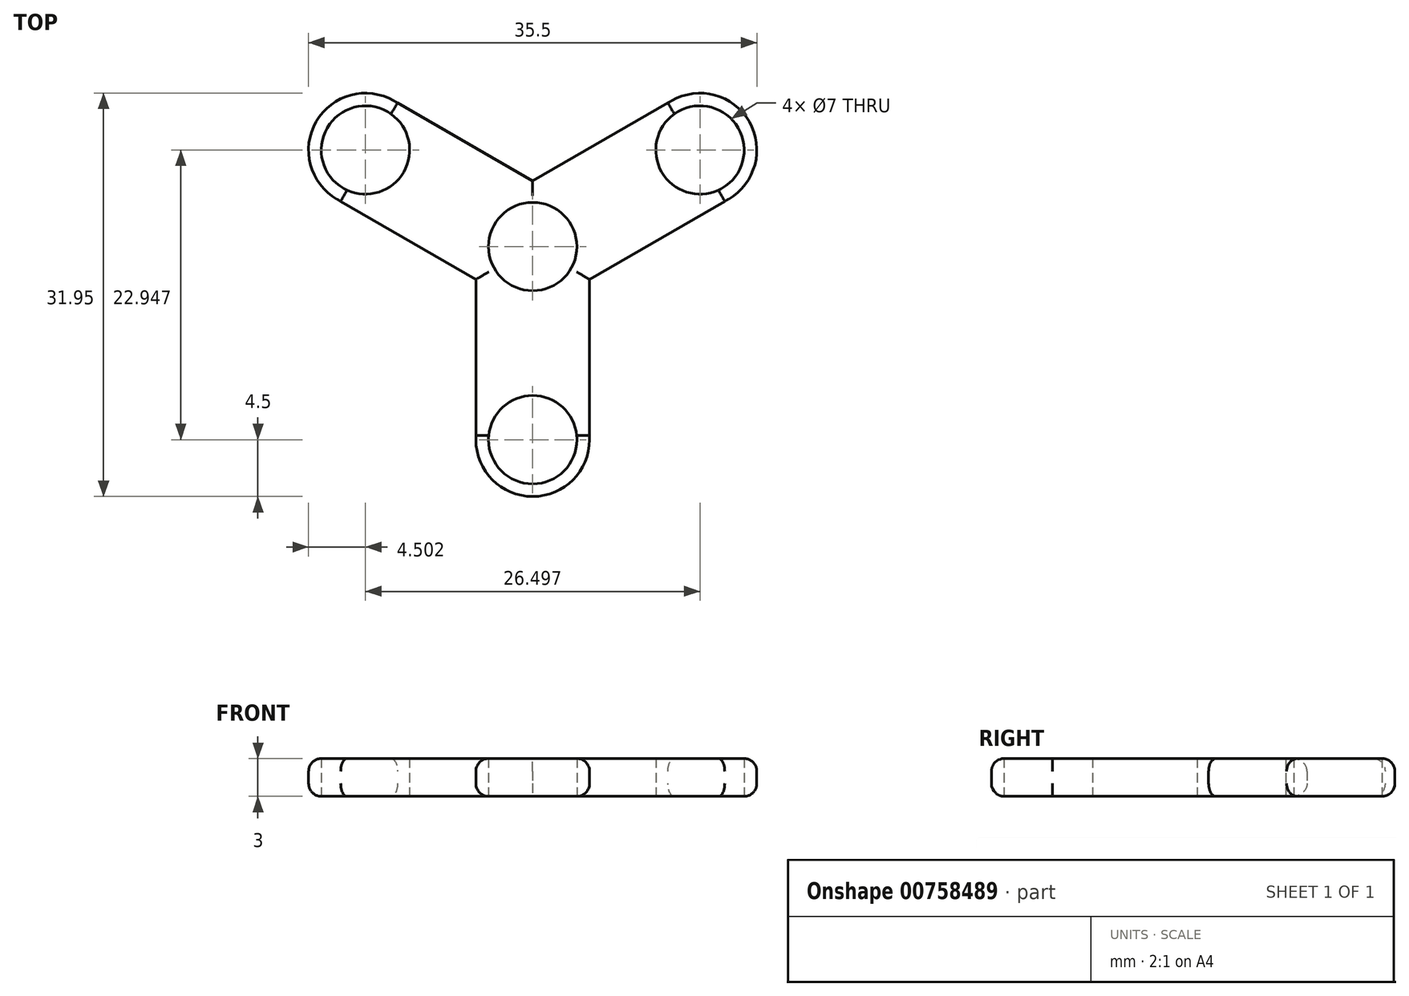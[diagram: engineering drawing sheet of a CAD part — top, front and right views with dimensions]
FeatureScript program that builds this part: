
annotation { "Feature Type Name" : "Feature", "Feature Type Description" : "" }
export const myFeature = defineFeature(function(context is Context, id is Id, definition is map)
    precondition{}
    {
        {
            var Q0;
            Q0=qCreatedBy(makeId("Top.planeOp"),FACE);
            var sketch = newSketch(context, id + "F0", { "sketchPlane" : qUnion([Q0])});
            skPoint(sketch, "E0.0.midPoint", {"position": v(6.35, -3.67) * mm});
            skLineSegment(sketch, "E1", {"start": v(-58.3, 0) * mm, "end": v(49.78, 0) * mm, "construction": true});
            skCircle(sketch, "E2", {"center": v(-13.25, 10.25) * mm, "radius": 4.5 * mm});
            skCircle(sketch, "E3", {"center": v(13.25, 10.25) * mm, "radius": 4.5 * mm});
            skCircle(sketch, "E4", {"center": v(0, -12.7) * mm, "radius": 4.5 * mm});
            skLineSegment(sketch, "E5", {"start": v(-4.5, -12.7) * mm, "end": v(-4.5, 0) * mm});
            skPoint(sketch, "E5.endSnap0", {"position": v(-4.26, 0) * mm});
            skLineSegment(sketch, "E6", {"start": v(4.5, -12.7) * mm, "end": v(4.5, 0) * mm});
            skLineSegment(sketch, "E7", {"start": v(4.5, 0) * mm, "end": v(15.5, 6.35) * mm});
            skLineSegment(sketch, "E8", {"start": v(11, 14.14) * mm, "end": v(0, 7.8) * mm});
            skLineSegment(sketch, "E9", {"start": v(0, 7.8) * mm, "end": v(-11, 14.14) * mm});
            skLineSegment(sketch, "E10", {"start": v(-15.5, 6.35) * mm, "end": v(-4.5, 0) * mm});
            skCircle(sketch, "E11", {"center": v(-13.25, 10.25) * mm, "radius": 3.5 * mm});
            skCircle(sketch, "E12", {"center": v(13.25, 10.25) * mm, "radius": 3.5 * mm});
            skCircle(sketch, "E13", {"center": v(0, -12.7) * mm, "radius": 3.5 * mm});
            skCircle(sketch, "E14.cCircle", {"center": v(0, 2.6) * mm, "radius": 7.65 * mm, "construction": true});
            skLineSegment(sketch, "E14.0", {"start": v(-13.25, 10.25) * mm, "end": v(13.25, 10.25) * mm});
            skLineSegment(sketch, "E14.1", {"start": v(13.25, 10.25) * mm, "end": v(0, -12.7) * mm});
            skLineSegment(sketch, "E14.2", {"start": v(0, -12.7) * mm, "end": v(-13.25, 10.25) * mm});
            skPoint(sketch, "E14.0.midPoint", {"position": v(0, 10.25) * mm});
            skCircle(sketch, "E15", {"center": v(0, 2.6) * mm, "radius": 3.5 * mm});
            skSolve(sketch);
        }
        {
            var Q0;
            Q0=makeQuery(id+"F0.imprint","IMPRINT",FACE,{"disambiguationData":[TD([[makeQuery(id+"F0.imprint","IMPRINT",EDGE,{"derivedFrom":sQuery(id+"F0.wireOp",EDGE,"E11")}),-1.0]])]});
            var Q1;
            Q1=makeQuery(id+"F0.imprint","IMPRINT",FACE,{"disambiguationData":[TD([[makeQuery(id+"F0.imprint","IMPRINT",EDGE,{"derivedFrom":sQuery(id+"F0.wireOp",EDGE,"E12")}),-1.0]])]});
            var Q2;
            Q2=makeQuery(id+"F0.imprint","IMPRINT",FACE,{"disambiguationData":[TD([[makeQuery(id+"F0.imprint","IMPRINT",EDGE,{"derivedFrom":sQuery(id+"F0.wireOp",EDGE,"E13")}),-1.0]])]});
            var Q3;
            Q3=makeQuery(id+"F0.imprint","IMPRINT",FACE,{"disambiguationData":[TD([[makeQuery(id+"F0.imprint","IMPRINT",EDGE,{"derivedFrom":sQuery(id+"F0.wireOp",EDGE,"E15")}),-1.0]])]});
            var Q4;
            {var subQ0=sQuery(id+"F0.wireOp",EDGE,"E5");var subQ1=sQuery(id+"F0.wireOp",EDGE,"E4");var subQ2=makeQuery(id+"F0.imprint","INTERSECT",VERTEX,{"derivedFrom":[subQ1,subQ0]});Q4=makeQuery(id+"F0.imprint","IMPRINT",FACE,{"disambiguationData":[TD([[makeQuery(id+"F0.imprint","IMPRINT",EDGE,{"disambiguationData":[TD([[subQ2,1.0]])],"derivedFrom":subQ1}),-1.0]])]});}
            var Q5;
            {var subQ0=sQuery(id+"F0.wireOp",EDGE,"E6");var subQ1=sQuery(id+"F0.wireOp",EDGE,"E4");var subQ2=makeQuery(id+"F0.imprint","INTERSECT",VERTEX,{"derivedFrom":[subQ1,subQ0]});Q5=makeQuery(id+"F0.imprint","IMPRINT",FACE,{"disambiguationData":[TD([[makeQuery(id+"F0.imprint","IMPRINT",EDGE,{"disambiguationData":[TD([[subQ2,-1.0]])],"derivedFrom":subQ1}),-1.0]])]});}
            var Q6;
            {var subQ5=sQuery(id+"F0.wireOp",EDGE,"E4");var subQ7=makeQuery(id+"F0.imprint","INTERSECT",VERTEX,{"derivedFrom":[subQ5,sQuery(id+"F0.wireOp",EDGE,"E6")]});Q6=makeQuery(id+"F0.imprint","IMPRINT",FACE,{"disambiguationData":[TD([[makeQuery(id+"F0.imprint","IMPRINT",EDGE,{"disambiguationData":[TD([[subQ7,-1.0]])],"derivedFrom":subQ5}),1.0]])]});}
            var Q7;
            {var subQ5=sQuery(id+"F0.wireOp",EDGE,"E3");var subQ8=makeQuery(id+"F0.imprint","INTERSECT",VERTEX,{"derivedFrom":[subQ5,sQuery(id+"F0.wireOp",EDGE,"E8")]});Q7=makeQuery(id+"F0.imprint","IMPRINT",FACE,{"disambiguationData":[TD([[makeQuery(id+"F0.imprint","IMPRINT",EDGE,{"disambiguationData":[TD([[subQ8,-1.0]])],"derivedFrom":subQ5}),1.0]])]});}
            var Q8;
            {var subQ0=sQuery(id+"F0.wireOp",EDGE,"E7");var subQ1=sQuery(id+"F0.wireOp",EDGE,"E3");var subQ2=makeQuery(id+"F0.imprint","INTERSECT",VERTEX,{"derivedFrom":[subQ1,subQ0]});Q8=makeQuery(id+"F0.imprint","IMPRINT",FACE,{"disambiguationData":[TD([[makeQuery(id+"F0.imprint","IMPRINT",EDGE,{"disambiguationData":[TD([[subQ2,1.0]])],"derivedFrom":subQ1}),-1.0]])]});}
            var Q9;
            {var subQ0=sQuery(id+"F0.wireOp",EDGE,"E8");var subQ1=sQuery(id+"F0.wireOp",EDGE,"E3");var subQ2=makeQuery(id+"F0.imprint","INTERSECT",VERTEX,{"derivedFrom":[subQ1,subQ0]});Q9=makeQuery(id+"F0.imprint","IMPRINT",FACE,{"disambiguationData":[TD([[makeQuery(id+"F0.imprint","IMPRINT",EDGE,{"disambiguationData":[TD([[subQ2,-1.0]])],"derivedFrom":subQ1}),-1.0]])]});}
            var Q10;
            {var subQ0=sQuery(id+"F0.wireOp",EDGE,"E9");var subQ1=sQuery(id+"F0.wireOp",EDGE,"E2");var subQ2=makeQuery(id+"F0.imprint","INTERSECT",VERTEX,{"derivedFrom":[subQ1,subQ0]});Q10=makeQuery(id+"F0.imprint","IMPRINT",FACE,{"disambiguationData":[TD([[makeQuery(id+"F0.imprint","IMPRINT",EDGE,{"disambiguationData":[TD([[subQ2,1.0]])],"derivedFrom":subQ1}),-1.0]])]});}
            var Q11;
            {var subQ0=sQuery(id+"F0.wireOp",EDGE,"E10");var subQ1=sQuery(id+"F0.wireOp",EDGE,"E2");var subQ2=makeQuery(id+"F0.imprint","INTERSECT",VERTEX,{"derivedFrom":[subQ1,subQ0]});Q11=makeQuery(id+"F0.imprint","IMPRINT",FACE,{"disambiguationData":[TD([[makeQuery(id+"F0.imprint","IMPRINT",EDGE,{"disambiguationData":[TD([[subQ2,-1.0]])],"derivedFrom":subQ1}),-1.0]])]});}
            var Q12;
            {var subQ5=sQuery(id+"F0.wireOp",EDGE,"E2");var subQ8=makeQuery(id+"F0.imprint","INTERSECT",VERTEX,{"derivedFrom":[subQ5,sQuery(id+"F0.wireOp",EDGE,"E9")]});Q12=makeQuery(id+"F0.imprint","IMPRINT",FACE,{"disambiguationData":[TD([[makeQuery(id+"F0.imprint","IMPRINT",EDGE,{"disambiguationData":[TD([[subQ8,1.0]])],"derivedFrom":subQ5}),1.0]])]});}
            extrude(context, id + "F1", {"entities" : qUnion([Q0, Q1, Q2, Q3, Q4, Q5, Q6, Q7, Q8, Q9, Q10, Q11, Q12]), "depth" : 3 * mm, "offsetDistance" : 25.4 * mm});
        }
        {
            var Q0;
            Q0=makeQuery(id+"F1.opExtrude","CAP_EDGE",EDGE,{"disambiguationData":[OSD([sQuery(id+"F0.wireOp",EDGE,"E8")])],"isStart":false});
            var Q1;
            Q1=makeQuery(id+"F1.opExtrude","CAP_EDGE",EDGE,{"disambiguationData":[OSD([sQuery(id+"F0.wireOp",EDGE,"E7")])],"isStart":false});
            var Q2;
            Q2=makeQuery(id+"F1.opExtrude","CAP_EDGE",EDGE,{"disambiguationData":[OSD([sQuery(id+"F0.wireOp",EDGE,"E9")])],"isStart":false});
            var Q3;
            Q3=makeQuery(id+"F1.opExtrude","CAP_EDGE",EDGE,{"disambiguationData":[OSD([sQuery(id+"F0.wireOp",EDGE,"E10")])],"isStart":false});
            var Q4;
            Q4=makeQuery(id+"F1.opExtrude","CAP_EDGE",EDGE,{"disambiguationData":[OSD([sQuery(id+"F0.wireOp",EDGE,"E5")])],"isStart":false});
            var Q5;
            Q5=makeQuery(id+"F1.opExtrude","CAP_EDGE",EDGE,{"disambiguationData":[OSD([sQuery(id+"F0.wireOp",EDGE,"E6")])],"isStart":false});
            var Q6;
            Q6=makeQuery(id+"F1.opExtrude","CAP_EDGE",EDGE,{"disambiguationData":[OSD([sQuery(id+"F0.wireOp",EDGE,"E4")])],"isStart":false});
            var Q7;
            Q7=makeQuery(id+"F1.opExtrude","CAP_EDGE",EDGE,{"disambiguationData":[OSD([sQuery(id+"F0.wireOp",EDGE,"E2")])],"isStart":false});
            var Q8;
            Q8=makeQuery(id+"F1.opExtrude","CAP_EDGE",EDGE,{"disambiguationData":[OSD([sQuery(id+"F0.wireOp",EDGE,"E3")])],"isStart":false});
            var Q9;
            Q9=makeQuery(id+"F1.opExtrude","CAP_EDGE",EDGE,{"disambiguationData":[OSD([sQuery(id+"F0.wireOp",EDGE,"E10")])],"isStart":true});
            var Q10;
            Q10=makeQuery(id+"F1.opExtrude","CAP_EDGE",EDGE,{"disambiguationData":[OSD([sQuery(id+"F0.wireOp",EDGE,"E5")])],"isStart":true});
            var Q11;
            Q11=makeQuery(id+"F1.opExtrude","CAP_EDGE",EDGE,{"disambiguationData":[OSD([sQuery(id+"F0.wireOp",EDGE,"E6")])],"isStart":true});
            var Q12;
            Q12=makeQuery(id+"F1.opExtrude","CAP_EDGE",EDGE,{"disambiguationData":[OSD([sQuery(id+"F0.wireOp",EDGE,"E7")])],"isStart":true});
            var Q13;
            Q13=makeQuery(id+"F1.opExtrude","CAP_EDGE",EDGE,{"disambiguationData":[OSD([sQuery(id+"F0.wireOp",EDGE,"E3")])],"isStart":true});
            var Q14;
            Q14=makeQuery(id+"F1.opExtrude","CAP_EDGE",EDGE,{"disambiguationData":[OSD([sQuery(id+"F0.wireOp",EDGE,"E8")])],"isStart":true});
            var Q15;
            Q15=makeQuery(id+"F1.opExtrude","CAP_EDGE",EDGE,{"disambiguationData":[OSD([sQuery(id+"F0.wireOp",EDGE,"E4")])],"isStart":true});
            var Q16;
            Q16=makeQuery(id+"F1.opExtrude","CAP_EDGE",EDGE,{"disambiguationData":[OSD([sQuery(id+"F0.wireOp",EDGE,"E2")])],"isStart":true});
            var Q17;
            Q17=makeQuery(id+"F1.opExtrude","CAP_EDGE",EDGE,{"disambiguationData":[OSD([sQuery(id+"F0.wireOp",EDGE,"E9")])],"isStart":true});
            fillet(context, id + "F2", {"entities" : qUnion([Q0, Q1, Q2, Q3, Q4, Q5, Q6, Q7, Q8, Q9, Q10, Q11, Q12, Q13, Q14, Q15, Q16, Q17]), "radius" : 1.02 * mm, "tangentPropagation" : true, "allowEdgeOverflow" : false});
        }
    });
